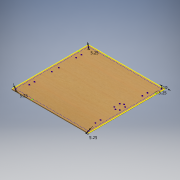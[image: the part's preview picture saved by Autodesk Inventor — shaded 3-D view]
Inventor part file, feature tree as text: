
AUTODESK INVENTOR PART (.ipt)
format: ipt  version: 2019 (Build 230136000, 136)  size: 165,376 bytes
history: native  units: in
note: dims shown in document units (in); Inventor stores cm internally (conversion verified against a paired STEP export)
features: extrude x2, sketch x1
ambient origin geometry x8: Origin, YZ Plane, XZ Plane, XY Plane, X Axis, Y Axis, Z Axis, Center Point
bodies: Solid1 (feature_tree)
feature tree (3):
  extrude  "Extrusion1"  Depth=0.3937in
  extrude  "Extrusion2"  Depth=0.3937in
  sketch  "Sketch1"  dims[d0=17.3228in d1=12.5984in d2=12.5984in d3=17.3228in d4=0.1969in d5=0.0in d10=0.1969in d11=0.0in d28=0.2067in d29=0.2067in d30=0.2067in d31=0.2067in d32=0.3937in]
